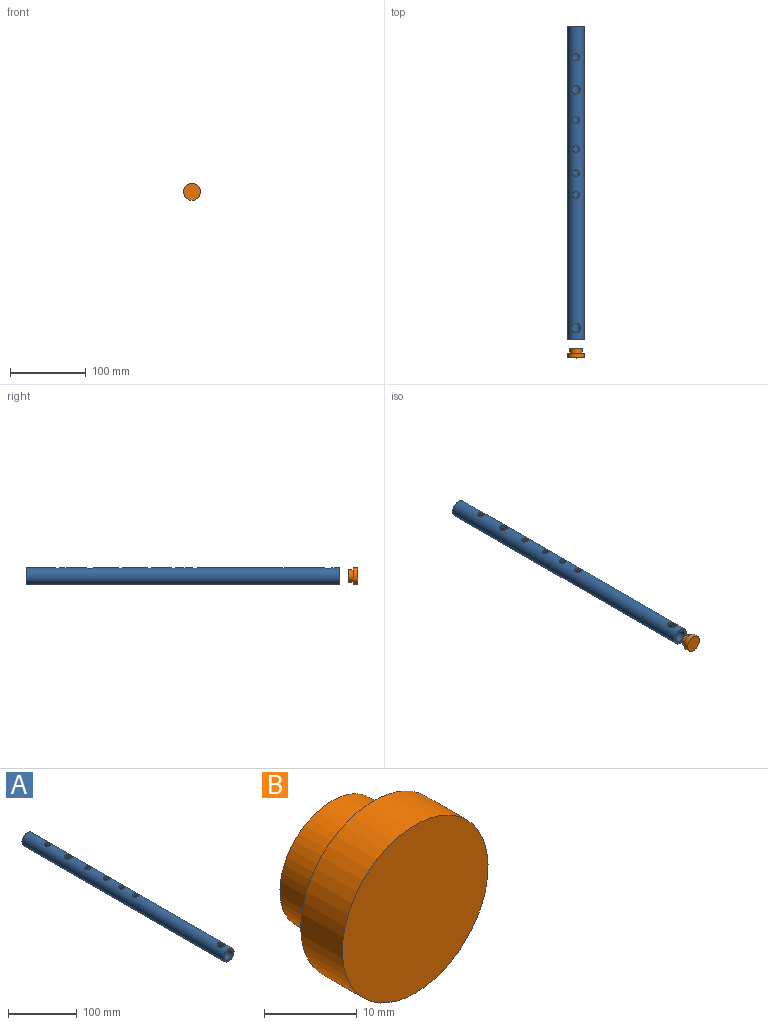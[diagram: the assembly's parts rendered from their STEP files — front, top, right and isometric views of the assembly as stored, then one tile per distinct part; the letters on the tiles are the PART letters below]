
ASSEMBLY  parts=2 mates=1
PART A: 11 faces, bbox 22.2x412.8x22.2 mm
  f0: cylinder r=7.94mm len=412.75mm, axis (0,1,0), area 20036.8mm2, adj f2,f3,f4,f5,f6,f7,f8,f9
  f1: cylinder r=11.11mm len=412.75mm, axis (0,1,0), area 28287.4mm2, adj f2,f3,f4,f5,f6,f7,f8,f9
  f2: plane 22.23x22.23mm, normal (0,-1,0), area 190mm2, adj f0,f1
  f3: plane 22.23x22.23mm, normal (0,1,0), area 190mm2, adj f0,f1
  f4: cylinder r=4.37mm len=8.73mm, axis (0,0,1), area 92.5mm2, adj f0,f1
  f5: cylinder r=4.56mm len=9.13mm, axis (0,0,1), area 97.3mm2, adj f0,f1
  f6: cylinder r=4.37mm len=8.73mm, axis (0,0,1), area 92.5mm2, adj f0,f1
  f7: cylinder r=5.56mm len=11.11mm, axis (0,0,1), area 123.3mm2, adj f0,f1
  f8: cylinder r=4.37mm len=8.73mm, axis (0,0,1), area 92.5mm2, adj f0,f1
  f9: extruded ~12.7x11.11mm, area 132.7mm2, adj f0,f1
  f10: cylinder r=4.56mm len=9.13mm, axis (0,0,1), area 97.3mm2, adj f0,f1
PART B: 5 faces, bbox 22.2x12.7x22.2 mm
  f0: cylinder r=7.94mm len=15.88mm, axis (0,1,0), area 316.7mm2, adj f1,f4
  f1: plane 15.88x15.88mm, normal (0,1,0), area 197.9mm2, adj f0
  f2: cylinder r=11.11mm len=22.23mm, axis (0,1,0), area 443.4mm2, adj f3,f4
  f3: plane 22.23x22.23mm, normal (0,-1,0), area 387.9mm2, adj f2
  f4: plane 22.23x22.23mm, normal (0,1,0), area 190mm2, adj f0,f2
PLACE A t=(-14.72,-6.54,-3.04)mm
PLACE B t=(-14.72,-430.66,-3.04)mm
MATE slider B.f0 <-> A.f0  axis (0,1,0) through (-14.72,-430.66,-3.04)mm
